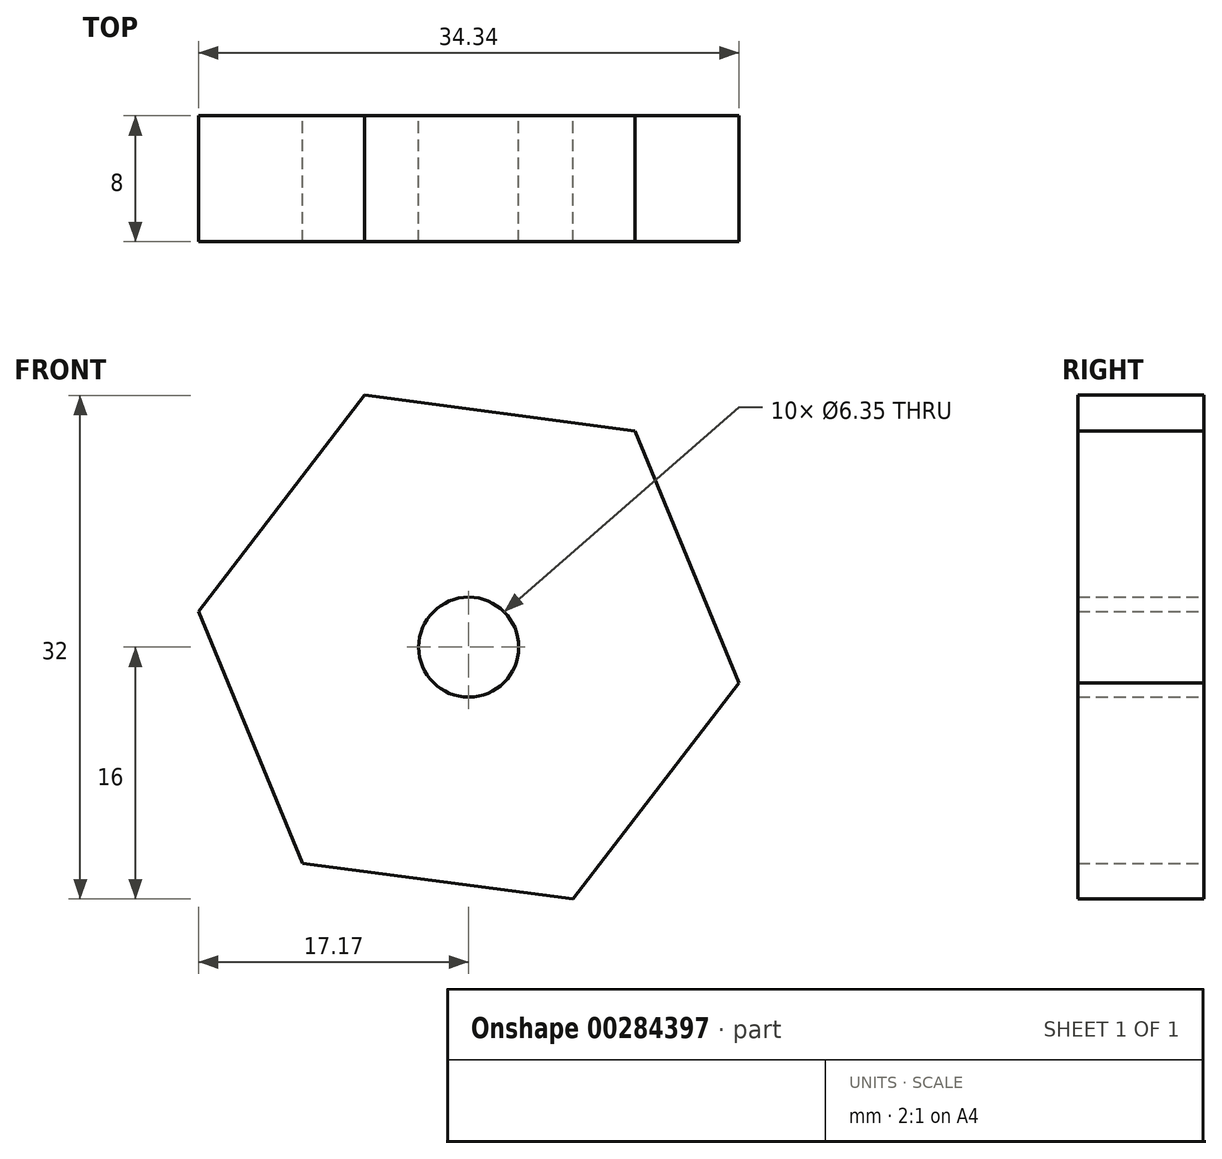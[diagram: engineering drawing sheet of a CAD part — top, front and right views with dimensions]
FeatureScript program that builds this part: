
annotation { "Feature Type Name" : "Feature", "Feature Type Description" : "" }
export const myFeature = defineFeature(function(context is Context, id is Id, definition is map)
    precondition{}
    {
        {
            var Q0;
            Q0=qCreatedBy(makeId("Front.planeOp"),FACE);
            var sketch = newSketch(context, id + "F0", { "sketchPlane" : qUnion([Q0])});
            skCircle(sketch, "E0.cCircle", {"center": v(0, 0) * mm, "radius": 15 * mm, "construction": true});
            skLineSegment(sketch, "E0.0", {"start": v(-6.62, 16) * mm, "end": v(10.55, 13.74) * mm});
            skLineSegment(sketch, "E0.1", {"start": v(10.55, 13.74) * mm, "end": v(17.17, -2.26) * mm});
            skLineSegment(sketch, "E0.2", {"start": v(17.17, -2.26) * mm, "end": v(6.62, -16) * mm});
            skLineSegment(sketch, "E0.3", {"start": v(6.62, -16) * mm, "end": v(-10.55, -13.74) * mm});
            skLineSegment(sketch, "E0.4", {"start": v(-10.55, -13.74) * mm, "end": v(-17.17, 2.26) * mm});
            skLineSegment(sketch, "E0.5", {"start": v(-17.17, 2.26) * mm, "end": v(-6.62, 16) * mm});
            skPoint(sketch, "E0.0.midPoint", {"position": v(1.96, 14.87) * mm});
            skCircle(sketch, "E1", {"center": v(0, 0) * mm, "radius": 3.18 * mm});
            skSolve(sketch);
        }
        {
            var Q0;
            Q0=makeQuery(id+"F0.imprint","IMPRINT",FACE,{"disambiguationData":[TD([[makeQuery(id+"F0.imprint","IMPRINT",EDGE,{"derivedFrom":sQuery(id+"F0.wireOp",EDGE,"E0.0")}),-1.0]])]});
            extrude(context, id + "F1", {"entities" : qUnion([Q0]), "depth" : 8 * mm});
        }
    });
